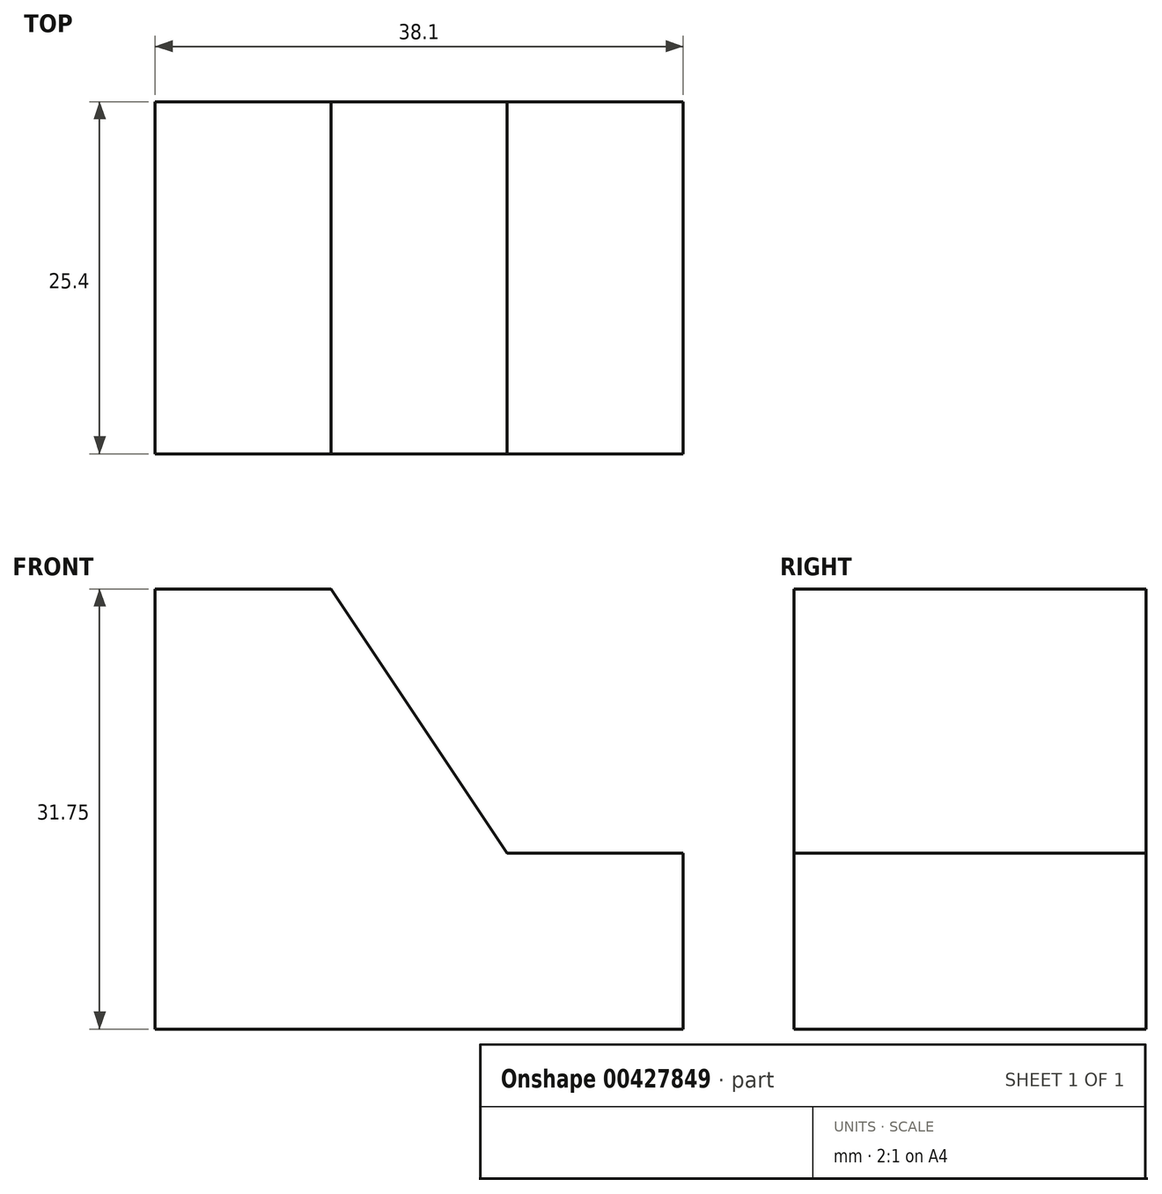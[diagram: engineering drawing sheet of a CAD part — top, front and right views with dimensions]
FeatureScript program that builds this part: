
annotation { "Feature Type Name" : "Feature", "Feature Type Description" : "" }
export const myFeature = defineFeature(function(context is Context, id is Id, definition is map)
    precondition{}
    {
        {
            var Q0;
            Q0=qCreatedBy(makeId("Front.planeOp"),FACE);
            var sketch = newSketch(context, id + "F0", { "sketchPlane" : qUnion([Q0])});
            skLineSegment(sketch, "E0", {"start": v(0, 0) * mm, "end": v(38.1, 0) * mm});
            skLineSegment(sketch, "E1", {"start": v(38.1, 0) * mm, "end": v(38.1, 12.7) * mm});
            skLineSegment(sketch, "E2", {"start": v(0, 0) * mm, "end": v(0, 31.75) * mm});
            skLineSegment(sketch, "E3", {"start": v(0, 31.75) * mm, "end": v(12.7, 31.75) * mm});
            skLineSegment(sketch, "E4", {"start": v(38.1, 12.7) * mm, "end": v(25.4, 12.7) * mm});
            skLineSegment(sketch, "E5", {"start": v(12.7, 31.75) * mm, "end": v(25.4, 12.7) * mm});
            skSolve(sketch);
        }
        {
            var Q0;
            Q0=makeQuery(id+"F0.imprint","IMPRINT",FACE,{"disambiguationData":[TD([[makeQuery(id+"F0.imprint","IMPRINT",EDGE,{"derivedFrom":sQuery(id+"F0.wireOp",EDGE,"E0")}),1.0]])]});
            extrude(context, id + "F1", {"entities" : qUnion([Q0]), "depth" : 25.4 * mm});
        }
    });
